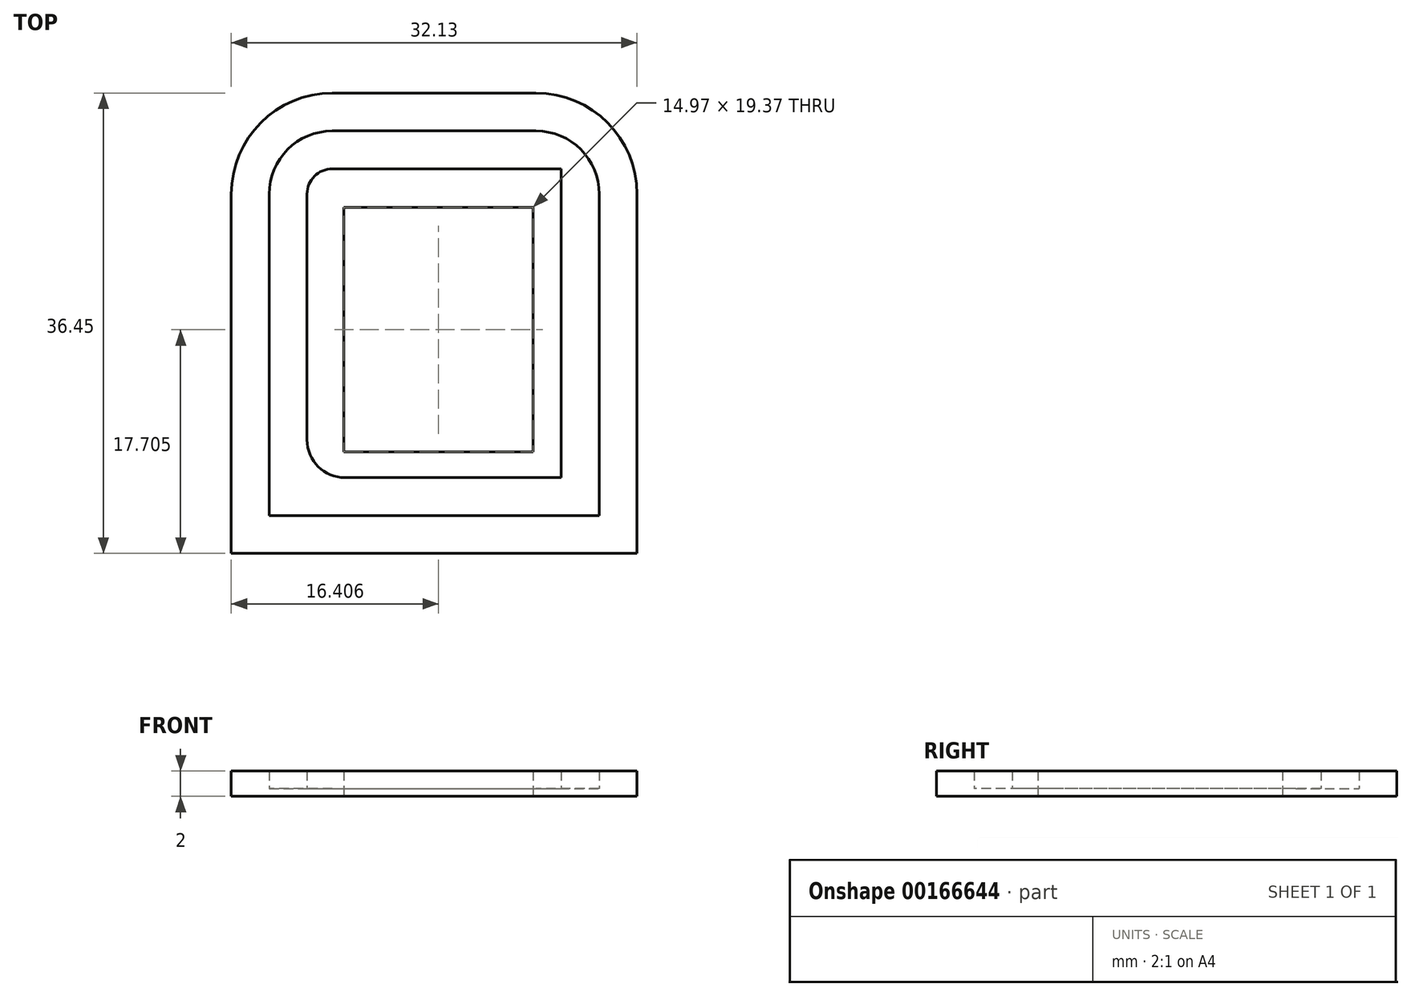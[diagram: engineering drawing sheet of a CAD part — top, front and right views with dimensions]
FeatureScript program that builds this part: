
annotation { "Feature Type Name" : "Feature", "Feature Type Description" : "" }
export const myFeature = defineFeature(function(context is Context, id is Id, definition is map)
    precondition{}
    {
        {
            var Q0;
            Q0=qCreatedBy(makeId("Top.planeOp"),FACE);
            var sketch = newSketch(context, id + "F0", { "sketchPlane" : qUnion([Q0])});
            skLineSegment(sketch, "E0.bottom", {"start": v(-29.73, 25.84) * mm, "end": v(-13.6, 25.84) * mm});
            skLineSegment(sketch, "E0.top", {"start": v(-37.73, -10.61) * mm, "end": v(-5.6, -10.61) * mm});
            skLineSegment(sketch, "E0.left", {"start": v(-37.73, 17.84) * mm, "end": v(-37.73, -10.61) * mm});
            skLineSegment(sketch, "E0.right", {"start": v(-5.6, 17.84) * mm, "end": v(-5.6, -10.61) * mm});
            skLineSegment(sketch, "E1.bottom", {"start": v(-29.73, 22.84) * mm, "end": v(-13.6, 22.84) * mm});
            skLineSegment(sketch, "E1.top", {"start": v(-34.73, -7.61) * mm, "end": v(-8.6, -7.61) * mm});
            skLineSegment(sketch, "E1.left", {"start": v(-34.73, 17.84) * mm, "end": v(-34.73, -7.61) * mm});
            skLineSegment(sketch, "E1.right", {"start": v(-8.6, 17.84) * mm, "end": v(-8.6, -7.61) * mm});
            skPoint(sketch, "E2.visualSharp", {"position": v(-8.6, 22.84) * mm});
            skArc(sketch, "E2.filletArc", {"start": v(-8.6, 17.84) * mm, "mid": v(-10.06, 21.38) * mm, "end": v(-13.6, 22.84) * mm});
            skPoint(sketch, "E3.visualSharp", {"position": v(-34.73, 22.84) * mm});
            skArc(sketch, "E3.filletArc", {"start": v(-29.73, 22.84) * mm, "mid": v(-33.27, 21.38) * mm, "end": v(-34.73, 17.84) * mm});
            skLineSegment(sketch, "E4.0", {"start": v(-29.73, 19.84) * mm, "end": v(-11.6, 19.84) * mm});
            skLineSegment(sketch, "E4.1", {"start": v(-31.73, 17.84) * mm, "end": v(-31.73, -1.61) * mm});
            skLineSegment(sketch, "E4.2", {"start": v(-28.73, -4.61) * mm, "end": v(-11.6, -4.61) * mm});
            skLineSegment(sketch, "E4.3", {"start": v(-11.6, 19.84) * mm, "end": v(-11.6, -4.61) * mm});
            skPoint(sketch, "E5.visualSharp", {"position": v(-31.73, 19.84) * mm});
            skArc(sketch, "E5.filletArc", {"start": v(-29.73, 19.84) * mm, "mid": v(-31.15, 19.26) * mm, "end": v(-31.73, 17.84) * mm});
            skPoint(sketch, "E6.visualSharp", {"position": v(-31.73, -4.61) * mm});
            skArc(sketch, "E6.filletArc", {"start": v(-31.73, -1.61) * mm, "mid": v(-30.85, -3.74) * mm, "end": v(-28.73, -4.61) * mm});
            skLineSegment(sketch, "E7.bottom", {"start": v(-28.81, 16.78) * mm, "end": v(-13.84, 16.78) * mm});
            skLineSegment(sketch, "E7.top", {"start": v(-28.81, -2.6) * mm, "end": v(-13.84, -2.6) * mm});
            skLineSegment(sketch, "E7.left", {"start": v(-28.81, 16.78) * mm, "end": v(-28.81, -2.6) * mm});
            skLineSegment(sketch, "E7.right", {"start": v(-13.84, 16.78) * mm, "end": v(-13.84, -2.6) * mm});
            skPoint(sketch, "E8.visualSharp", {"position": v(-37.73, 25.84) * mm});
            skArc(sketch, "E8.filletArc", {"start": v(-29.73, 25.84) * mm, "mid": v(-35.39, 23.5) * mm, "end": v(-37.73, 17.84) * mm});
            skPoint(sketch, "E9.visualSharp", {"position": v(-5.6, 25.84) * mm});
            skArc(sketch, "E9.filletArc", {"start": v(-5.6, 17.84) * mm, "mid": v(-7.94, 23.5) * mm, "end": v(-13.6, 25.84) * mm});
            skSolve(sketch);
        }
        {
            var Q0;
            Q0=makeQuery(id+"F0.imprint","IMPRINT",FACE,{"disambiguationData":[TD([[makeQuery(id+"F0.imprint","IMPRINT",EDGE,{"derivedFrom":sQuery(id+"F0.wireOp",EDGE,"E1.bottom")}),-1.0]])]});
            extrude(context, id + "F1", {"entities" : qUnion([Q0]), "depth" : 0.6 * mm});
        }
        {
            var Q0;
            Q0=makeQuery(id+"F0.imprint","IMPRINT",FACE,{"disambiguationData":[TD([[makeQuery(id+"F0.imprint","IMPRINT",EDGE,{"derivedFrom":sQuery(id+"F0.wireOp",EDGE,"E0.bottom")}),-1.0]])]});
            var Q1;
            Q1=makeQuery(id+"F0.imprint","IMPRINT",FACE,{"disambiguationData":[TD([[makeQuery(id+"F0.imprint","IMPRINT",EDGE,{"derivedFrom":sQuery(id+"F0.wireOp",EDGE,"E4.0")}),-1.0]])]});
            extrude(context, id + "F2", {"entities" : qUnion([Q0, Q1]), "operationType" : NewBodyOperationType.ADD, "depth" : 2 * mm});
        }
    });
